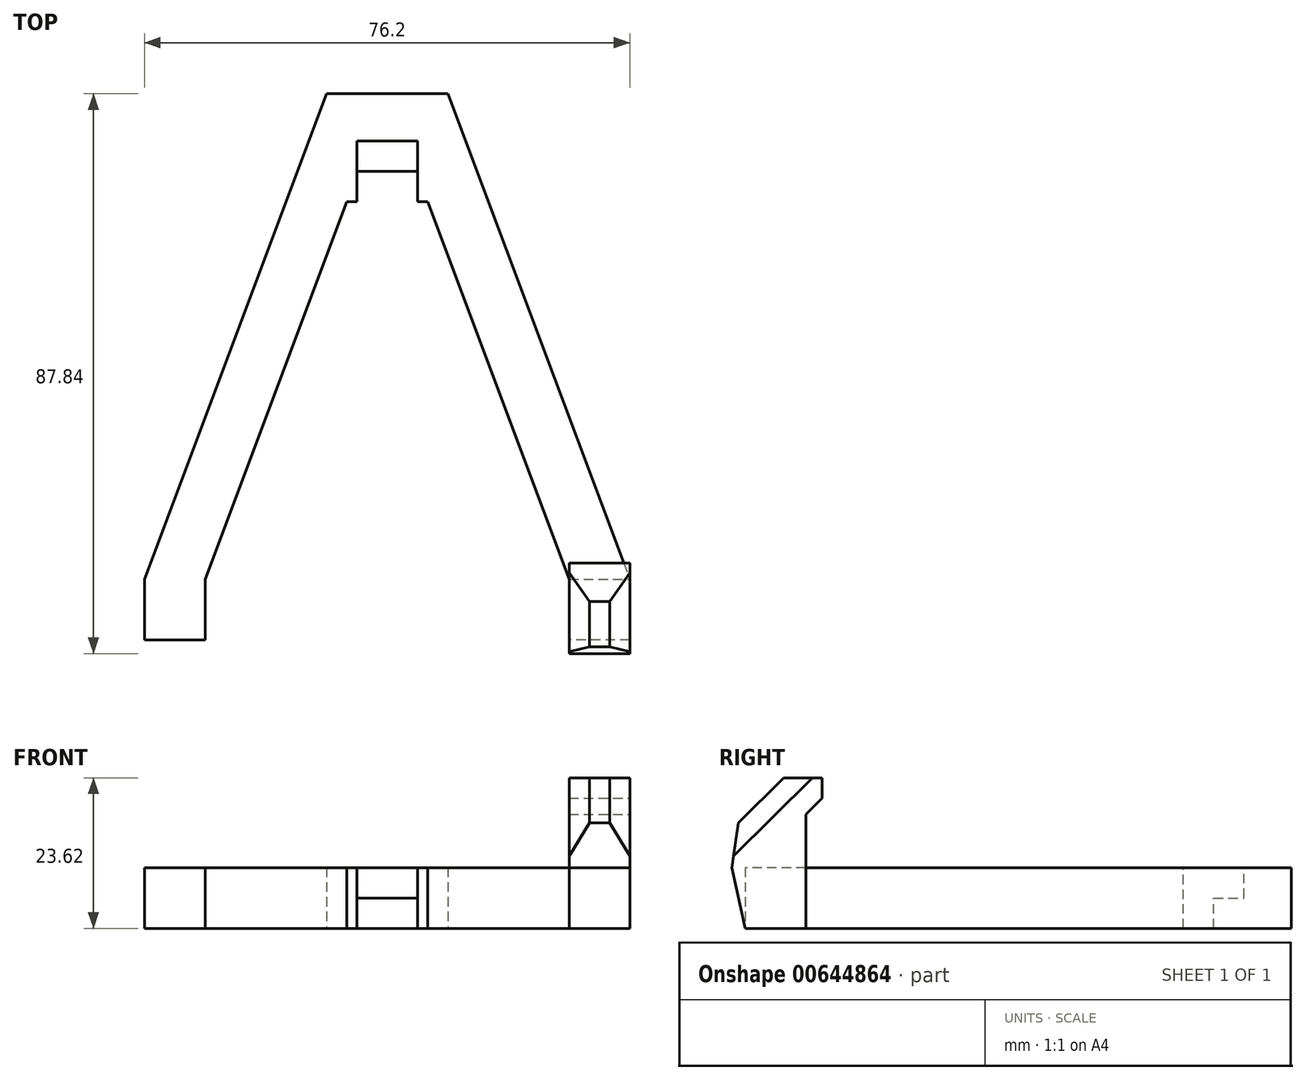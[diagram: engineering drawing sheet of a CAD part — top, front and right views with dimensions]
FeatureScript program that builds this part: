
annotation { "Feature Type Name" : "Feature", "Feature Type Description" : "" }
export const myFeature = defineFeature(function(context is Context, id is Id, definition is map)
    precondition{}
    {
        {
            var Q0;
            Q0=qCreatedBy(makeId("Top.planeOp"),FACE);
            var sketch = newSketch(context, id + "F0", { "sketchPlane" : qUnion([Q0])});
            skLineSegment(sketch, "E0", {"start": v(0, 0) * mm, "end": v(9.53, 0) * mm});
            skLineSegment(sketch, "E1", {"start": v(9.52, 0) * mm, "end": v(38.1, -76.2) * mm});
            skLineSegment(sketch, "E2", {"start": v(38.1, -76.2) * mm, "end": v(38.1, -85.73) * mm});
            skLineSegment(sketch, "E3", {"start": v(38.1, -85.73) * mm, "end": v(28.58, -85.73) * mm});
            skLineSegment(sketch, "E4", {"start": v(28.58, -85.73) * mm, "end": v(28.58, -76.2) * mm});
            skLineSegment(sketch, "E5", {"start": v(28.58, -76.2) * mm, "end": v(6.35, -16.93) * mm});
            skLineSegment(sketch, "E6", {"start": v(6.35, -16.93) * mm, "end": v(0, -16.93) * mm});
            skLineSegment(sketch, "E7", {"start": v(0, 0) * mm, "end": v(0, -16.93) * mm, "construction": true});
            skLineSegment(sketch, "E8.MirrorCS", {"start": v(0, 0) * mm, "end": v(-9.53, 0) * mm});
            skLineSegment(sketch, "E9.MirrorCS", {"start": v(-9.52, 0) * mm, "end": v(-38.1, -76.2) * mm});
            skLineSegment(sketch, "E10.MirrorCS", {"start": v(-38.1, -76.2) * mm, "end": v(-38.1, -85.73) * mm});
            skLineSegment(sketch, "E11.MirrorCS", {"start": v(-38.1, -85.73) * mm, "end": v(-28.58, -85.73) * mm});
            skLineSegment(sketch, "E12.MirrorCS", {"start": v(-28.58, -85.73) * mm, "end": v(-28.58, -76.2) * mm});
            skLineSegment(sketch, "E13.MirrorCS", {"start": v(-28.58, -76.2) * mm, "end": v(-6.35, -16.93) * mm});
            skLineSegment(sketch, "E14.MirrorCS", {"start": v(-6.35, -16.93) * mm, "end": v(0, -16.93) * mm});
            skSolve(sketch);
        }
        {
            var Q0;
            Q0 = qSketchRegion(id + "F0", true);
            extrude(context, id + "F1", {"entities" : qUnion([Q0]), "depth" : 9.52 * mm, "offsetDistance" : 25.4 * mm});
        }
        {
            var Q0;
            Q0=makeQuery(id+"F1.opExtrude","SWEPT_FACE",FACE,{"disambiguationData":[OSD([sQuery(id+"F0.wireOp",EDGE,"E2")])]});
            var sketch = newSketch(context, id + "F2", { "sketchPlane" : qUnion([Q0])});
            skLineSegment(sketch, "E15", {"start": v(-76.2, 9.53) * mm, "end": v(-76.2, 20.45) * mm});
            skLineSegment(sketch, "E16", {"start": v(-76.2, 20.45) * mm, "end": v(-73.66, 20.45) * mm});
            skLineSegment(sketch, "E17", {"start": v(-73.66, 20.45) * mm, "end": v(-73.66, 23.62) * mm});
            skLineSegment(sketch, "E18", {"start": v(-73.66, 23.62) * mm, "end": v(-79.7, 23.62) * mm});
            skLineSegment(sketch, "E19", {"start": v(-86.78, 16.57) * mm, "end": v(-87.84, 9.53) * mm});
            skLineSegment(sketch, "E20", {"start": v(-87.84, 9.52) * mm, "end": v(-85.73, 0) * mm});
            skLineSegment(sketch, "E21", {"start": v(-73.66, 20.45) * mm, "end": v(-76.2, 17.9) * mm});
            skLineSegment(sketch, "E22", {"start": v(-79.7, 23.62) * mm, "end": v(-86.78, 16.57) * mm});
            skPoint(sketch, "E22.endSnap0", {"position": v(-86.78, 16.57) * mm});
            skSolve(sketch);
        }
        {
            var Q0;
            {var subQ0=sQuery(id+"F2.wireOp",EDGE,"E16");Q0=makeQuery(id+"F2.imprint","IMPRINT",FACE,{"disambiguationData":[TD([[makeQuery(id+"F2.imprint","IMPRINT",EDGE,{"derivedFrom":subQ0}),1.0]])]});}
            var Q1;
            {var subQ0=sQuery(id+"F2.wireOp",EDGE,"E16");Q1=makeQuery(id+"F2.imprint","IMPRINT",FACE,{"disambiguationData":[TD([[makeQuery(id+"F2.imprint","IMPRINT",EDGE,{"derivedFrom":subQ0}),-1.0]])]});}
            var Q2;
            Q2=makeQuery(id+"F1.opExtrude","SWEPT_FACE",FACE,{"disambiguationData":[OSD([sQuery(id+"F0.wireOp",EDGE,"E4")])]});
            extrude(context, id + "F3", {"entities" : qUnion([Q0, Q1]), "operationType" : NewBodyOperationType.ADD, "oppositeDirection" : true, "depth" : 9.52 * mm, "endBoundEntityFace" : qUnion([Q2]), "offsetDistance" : 25.4 * mm});
        }
        {
            var Q0;
            Q0=makeQuery(id+"F1.opExtrude","CAP_FACE",FACE,{"disambiguationData":[OSD([sQuery(id+"F0.wireOp",EDGE,"E0"),sQuery(id+"F0.wireOp",EDGE,"E1"),sQuery(id+"F0.wireOp",EDGE,"E2"),sQuery(id+"F0.wireOp",EDGE,"E3"),sQuery(id+"F0.wireOp",EDGE,"E4"),sQuery(id+"F0.wireOp",EDGE,"E5"),sQuery(id+"F0.wireOp",EDGE,"E6"),sQuery(id+"F0.wireOp",EDGE,"E8.MirrorCS"),sQuery(id+"F0.wireOp",EDGE,"E9.MirrorCS"),sQuery(id+"F0.wireOp",EDGE,"E10.MirrorCS"),sQuery(id+"F0.wireOp",EDGE,"E11.MirrorCS"),sQuery(id+"F0.wireOp",EDGE,"E12.MirrorCS"),sQuery(id+"F0.wireOp",EDGE,"E13.MirrorCS"),sQuery(id+"F0.wireOp",EDGE,"E14.MirrorCS")])],"isStart":false});
            var sketch = newSketch(context, id + "F4", { "sketchPlane" : qUnion([Q0])});
            skLineSegment(sketch, "E23.bottom", {"start": v(-4.76, -16.93) * mm, "end": v(4.76, -16.93) * mm});
            skLineSegment(sketch, "E23.top", {"start": v(-4.76, -7.4) * mm, "end": v(4.76, -7.4) * mm});
            skLineSegment(sketch, "E23.left", {"start": v(-4.76, -16.93) * mm, "end": v(-4.76, -7.4) * mm});
            skLineSegment(sketch, "E23.right", {"start": v(4.76, -16.93) * mm, "end": v(4.76, -7.4) * mm});
            skSolve(sketch);
        }
        {
            var Q0;
            Q0 = qSketchRegion(id + "F4", true);
            extrude(context, id + "F5", {"entities" : qUnion([Q0]), "operationType" : NewBodyOperationType.REMOVE, "oppositeDirection" : true, "depth" : 4.76 * mm, "offsetDistance" : 25.4 * mm});
        }
        {
            var Q0;
            Q0=makeQuery(id+"F5.boolean.opBoolean","COPY",FACE,{"derivedFrom":makeQuery(id+"F5.opExtrude","CAP_FACE",FACE,{"disambiguationData":[OSD([sQuery(id+"F4.wireOp",EDGE,"E23.bottom"),sQuery(id+"F4.wireOp",EDGE,"E23.top"),sQuery(id+"F4.wireOp",EDGE,"E23.left"),sQuery(id+"F4.wireOp",EDGE,"E23.right")])],"isStart":false})});
            var sketch = newSketch(context, id + "F6", { "sketchPlane" : qUnion([Q0])});
            skLineSegment(sketch, "E24.bottom", {"start": v(-4.76, -16.93) * mm, "end": v(4.76, -16.93) * mm});
            skLineSegment(sketch, "E24.top", {"start": v(-4.76, -12.17) * mm, "end": v(4.76, -12.17) * mm});
            skLineSegment(sketch, "E24.left", {"start": v(-4.76, -16.93) * mm, "end": v(-4.76, -12.17) * mm});
            skLineSegment(sketch, "E24.right", {"start": v(4.76, -16.93) * mm, "end": v(4.76, -12.17) * mm});
            skSolve(sketch);
        }
        {
            var Q0;
            Q0 = qSketchRegion(id + "F6", true);
            extrude(context, id + "F7", {"entities" : qUnion([Q0]), "operationType" : NewBodyOperationType.REMOVE, "endBound" : BoundingType.THROUGH_ALL, "oppositeDirection" : true, "depth" : 25.4 * mm, "offsetDistance" : 25.4 * mm});
        }
        {
            var Q0;
            Q0=makeQuery(id+"FLGe0Asmb3CKUwe_1.1.F3.opExtrude","CAP_EDGE",EDGE,{"disambiguationData":[OSD([sQuery(id+"F2.wireOp",EDGE,"E22")])],"isStart":false});
            var Q1;
            Q1=makeQuery(id+"FLGe0Asmb3CKUwe_1.1.F3.opExtrude","CAP_EDGE",EDGE,{"disambiguationData":[OSD([sQuery(id+"F2.wireOp",EDGE,"E22")])],"isStart":true});
            var Q2;
            Q2=makeQuery(id+"F3.opExtrude","CAP_EDGE",EDGE,{"disambiguationData":[OSD([sQuery(id+"F2.wireOp",EDGE,"E22")])],"isStart":true});
            var Q3;
            Q3=makeQuery(id+"F3.opExtrude","CAP_EDGE",EDGE,{"disambiguationData":[OSD([sQuery(id+"F2.wireOp",EDGE,"E22")])],"isStart":false});
            chamfer(context, id + "F8", {"entities" : qUnion([Q0, Q1, Q2, Q3]), "width" : 3.17 * mm, "tangentPropagation" : true});
        }
    });
